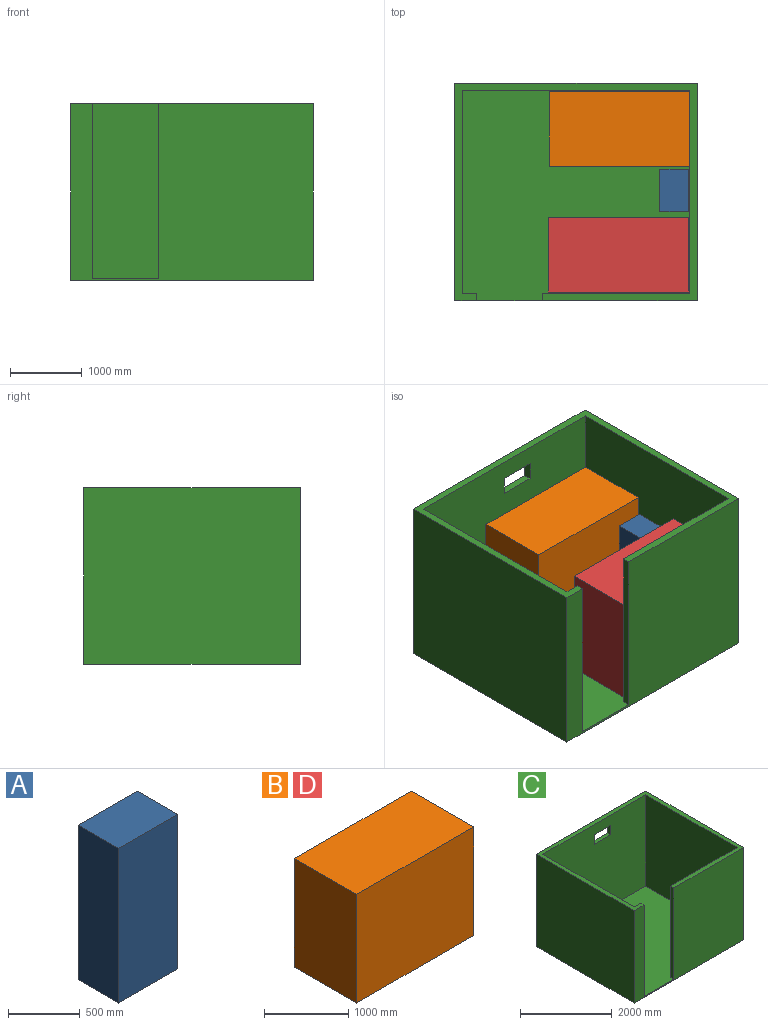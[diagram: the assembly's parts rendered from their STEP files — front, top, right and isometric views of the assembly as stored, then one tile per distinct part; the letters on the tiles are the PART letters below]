
ASSEMBLY  parts=4 mates=3
PART A: 6 faces, bbox 584.2x400.1x1320.8 mm
  f0: plane 1320.8x400.05mm, normal (1,0,0), area 528386mm2, adj f1,f3,f4,f5
  f1: plane 1320.8x584.2mm, normal (0,1,0), area 771611.4mm2, adj f0,f2,f4,f5
  f2: plane 1320.8x400.05mm, normal (-1,0,0), area 528386mm2, adj f1,f3,f4,f5
  f3: plane 1320.8x584.2mm, normal (0,-1,0), area 771611.4mm2, adj f0,f2,f4,f5
  f4: plane 584.2x400.05mm, normal (0,0,1), area 233709.2mm2, adj f0,f1,f2,f3
  f5: plane 584.2x400.05mm, normal (0,0,-1), area 233709.2mm2, adj f0,f1,f2,f3
PART B: 6 faces, bbox 1959x1041.4x1574.8 mm
  f0: plane 1574.8x1041.4mm, normal (1,0,0), area 1639996.7mm2, adj f1,f3,f4,f5
  f1: plane 1958.98x1574.8mm, normal (0,1,0), area 3084993.8mm2, adj f0,f2,f4,f5
  f2: plane 1574.8x1041.4mm, normal (-1,0,0), area 1639996.7mm2, adj f1,f3,f4,f5
  f3: plane 1958.98x1574.8mm, normal (0,-1,0), area 3084993.8mm2, adj f0,f2,f4,f5
  f4: plane 1958.98x1041.4mm, normal (0,0,1), area 2040076.6mm2, adj f0,f1,f2,f3
  f5: plane 1958.98x1041.4mm, normal (0,0,-1), area 2040076.6mm2, adj f0,f1,f2,f3
PART C: 18 faces, bbox 3378.2x3022.6x2463.8 mm
  f0: plane 3378.2x2463.8mm, normal (0,1,0), area 8194177.2mm2, adj f2,f3,f11,f12,f13,f14,f15,f17
  f1: plane 3175x2438.4mm, normal (0,-1,0), area 7612888mm2, adj f7,f8,f11,f12,f13,f14,f15,f16
  f2: plane 3022.6x2463.8mm, normal (1,0,0), area 7447081.9mm2, adj f0,f4,f11,f17
  f3: plane 3022.6x2463.8mm, normal (-1,0,0), area 7447081.9mm2, adj f0,f4,f11,f17
  f4: plane 3378.2x2463.8mm, normal (0,-1,0), area 6093536.2mm2, adj f2,f3,f5,f10,f11,f16,f17
  f5: plane 2438.4x101.6mm, normal (1,0,0), area 247741.4mm2, adj f4,f6,f11,f16
  f6: plane 2438.4x203.2mm, normal (0,1,0), area 495482.9mm2, adj f5,f7,f11,f16
  f7: plane 2819.4x2438.4mm, normal (1,0,0), area 6874825mm2, adj f1,f6,f11,f16
  f8: plane 2819.4x2438.4mm, normal (-1,0,0), area 6874825mm2, adj f1,f9,f11,f16
  f9: plane 2438.4x2057.4mm, normal (0,1,0), area 5016764.2mm2, adj f8,f10,f11,f16
  f10: plane 2438.4x101.6mm, normal (-1,0,0), area 247741.4mm2, adj f4,f9,f11,f16
  f11: plane 3378.2x3022.6mm, normal (0,0,1), area 1166449.3mm2, adj f0,f1,f2,f3,f4,f5,f6,f7
  f12: plane 508x101.6mm, normal (0,0,1), area 51612.8mm2, adj f0,f1,f13,f15
  f13: plane 254x101.6mm, normal (1,0,0), area 25806.4mm2, adj f0,f1,f12,f14
  f14: plane 508x101.6mm, normal (0,0,-1), area 51612.8mm2, adj f0,f1,f13,f15
  f15: plane 254x101.6mm, normal (-1,0,0), area 25806.4mm2, adj f0,f1,f12,f14
  f16: plane 3175x2921mm, normal (0,0,1), area 9044498mm2, adj f1,f4,f5,f6,f7,f8,f9,f10
  f17: plane 3378.2x3022.6mm, normal (0,0,-1), area 10210947.3mm2, adj f0,f2,f3,f4
PART D: same geometry as B
PLACE A rot(axis=(0,0,-1),90deg) t=(3166.19,-93.68,103.53)mm
PLACE B t=(2404.24,762.29,103.53)mm
PLACE C t=(1799.49,-115.67,103.53)mm fixed
PLACE D rot(axis=(0,0,-1),180deg) t=(2390.55,-988.71,103.53)mm
MATE planar D.f5 <-> C.f16  axis (0,0,-1) through (2390.55,-988.71,103.53)mm
MATE planar B.f5 <-> C.f16  axis (0,0,-1) through (2404.24,762.29,103.53)mm
MATE planar A.f5 <-> C.f16  axis (0,0,-1) through (3166.19,-93.68,103.53)mm
